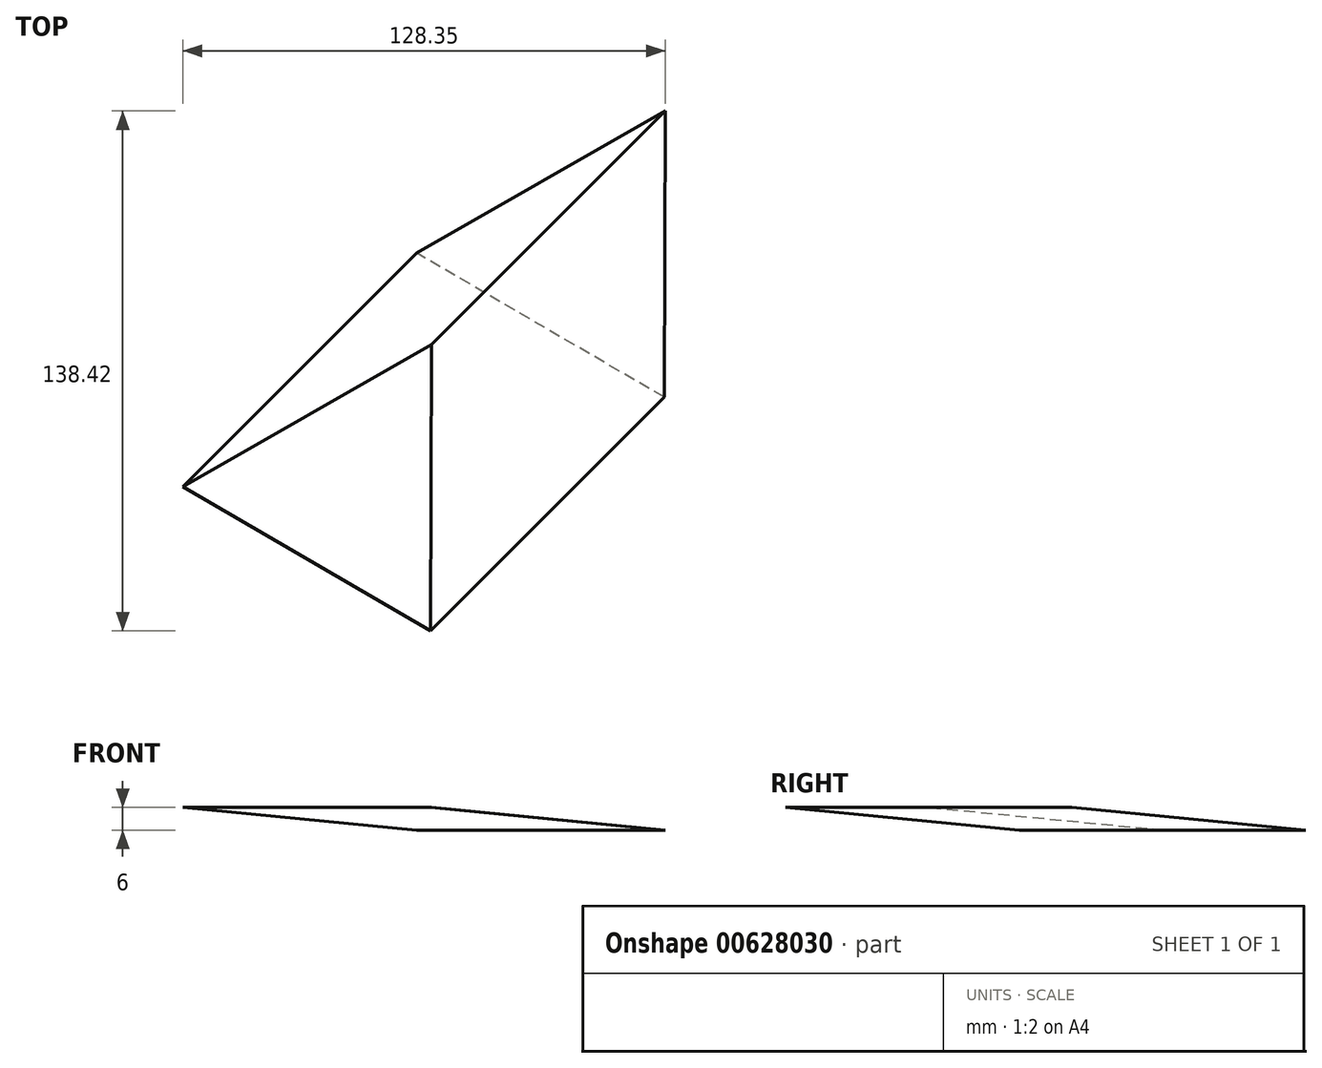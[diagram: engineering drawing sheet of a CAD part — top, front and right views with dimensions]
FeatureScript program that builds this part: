
annotation { "Feature Type Name" : "Feature", "Feature Type Description" : "" }
export const myFeature = defineFeature(function(context is Context, id is Id, definition is map)
    precondition{}
    {
        {
            assignVariable(context, id + "F0", {"name" : "l", "anyValue" : 6});
        }
        {
            var Q0;
            Q0=qCreatedBy(makeId("Top.planeOp"),FACE);
            var sketch = newSketch(context, id + "F1", { "sketchPlane" : qUnion([Q0])});
            skCircle(sketch, "E0.cCircle", {"center": v(0, 0) * mm, "radius": 22 * mm, "construction": true});
            skLineSegment(sketch, "E0.0", {"start": v(22.14, 38.02) * mm, "end": v(21.86, -38.18) * mm});
            skLineSegment(sketch, "E0.1", {"start": v(21.86, -38.18) * mm, "end": v(-44, 0.16) * mm});
            skLineSegment(sketch, "E0.2", {"start": v(-44, 0.16) * mm, "end": v(22.14, 38.02) * mm});
            skPoint(sketch, "E0.0.midPoint", {"position": v(22, -0.08) * mm});
            skSolve(sketch);
        }
        {
            var Q0;
            Q0=qCreatedBy(makeId("Right.planeOp"),FACE);
            var Q1;
            Q1=qCreatedBy(makeId("Front.planeOp"),FACE);
            cPlane(context, id + "F2", {"entities" : qUnion([Q0, Q1]), "cplaneType" : CPlaneType.MID_PLANE, "offset" : 25.4 * mm, "flipAlignment" : true, "width" : 152.4 * mm, "height" : 152.4 * mm});
        }
        {
            var Q0;
            Q0=qCreatedBy(makeId("Top.planeOp"),FACE);
            cPlane(context, id + "F3", {"entities" : qUnion([Q0]), "cplaneType" : CPlaneType.OFFSET, "offset" : (getVariable(context, 'l')) * mm, "width" : 152.4 * mm, "height" : 152.4 * mm});
        }
        {
            var Q0;
            Q0=qCreatedBy(id+"F2.planeOp",FACE);
            var sketch = newSketch(context, id + "F4", { "sketchPlane" : qUnion([Q0])});
            skLineSegment(sketch, "E1", {"start": v(0, 0) * mm, "end": v(-88.31, 152.96) * mm});
            skSolve(sketch);
        }
        {
            var Q0;
            Q0=qCreatedBy(id+"F3.planeOp",FACE);
            var sketch = newSketch(context, id + "F5", { "sketchPlane" : qUnion([Q0])});
            skLineSegment(sketch, "E2.0", {"start": v(-40.08, -24.2) * mm, "end": v(-40.36, -100.4) * mm});
            skLineSegment(sketch, "E3.0", {"start": v(-106.21, -62.05) * mm, "end": v(-40.08, -24.2) * mm});
            skLineSegment(sketch, "E4.0", {"start": v(-40.36, -100.4) * mm, "end": v(-106.21, -62.05) * mm});
            skCircle(sketch, "E5.0", {"center": v(-62.22, -62.22) * mm, "radius": 22 * mm, "construction": true});
            skSolve(sketch);
        }
        {
            var Q0;
            Q0=makeQuery(id+"F5.imprint","IMPRINT",FACE,{"disambiguationData":[TD([[makeQuery(id+"F5.imprint","IMPRINT",EDGE,{"derivedFrom":sQuery(id+"F5.wireOp",EDGE,"E2.0")}),-1.0]])]});
            var Q1;
            Q1=makeQuery(id+"F1.imprint","IMPRINT",FACE,{"disambiguationData":[TD([[makeQuery(id+"F1.imprint","IMPRINT",EDGE,{"derivedFrom":sQuery(id+"F1.wireOp",EDGE,"E0.0")}),-1.0]])]});
            var Q2;
            Q2=makeQuery(id+"F5.imprint","IMPRINT",FACE,{"disambiguationData":[TD([[makeQuery(id+"F5.imprint","IMPRINT",EDGE,{"derivedFrom":sQuery(id+"F5.wireOp",EDGE,"E2.0")}),-1.0]])]});
            var Q3;
            Q3=makeQuery(id+"F1.imprint","IMPRINT",FACE,{"disambiguationData":[TD([[makeQuery(id+"F1.imprint","IMPRINT",EDGE,{"derivedFrom":sQuery(id+"F1.wireOp",EDGE,"E0.0")}),-1.0]])]});
            var Q4;
            Q4=sQuery(id+"F1.wireOp",VERTEX,"E0.0.start");
            var Q5;
            Q5=sQuery(id+"F5.wireOp",VERTEX,"E3.0.end");
            var Q6;
            Q6=sQuery(id+"F1.wireOp",VERTEX,"E0.2.start");
            var Q7;
            Q7=sQuery(id+"F5.wireOp",VERTEX,"E4.0.end");
            var Q8;
            Q8=sQuery(id+"F1.wireOp",VERTEX,"E0.1.start");
            var Q9;
            Q9=sQuery(id+"F5.wireOp",VERTEX,"E4.0.start");
            loft(context, id + "F6", {"sheetProfilesArray" : [{ "sheetProfileEntities" : qUnion([Q0]) }, { "sheetProfileEntities" : qUnion([Q1]) }], "wireProfilesArray" : [{ "wireProfileEntities" : qUnion([Q2]) }, { "wireProfileEntities" : qUnion([Q3]) }], "connections" : [{ "connectionEntities" : qUnion([Q4, Q5, Q6, Q7, Q8, Q9]), "connectionEdgeQueries" : qUnion([]), "connectionEdgeParameters" : [] }]});
        }
        {
            var Q0;
            Q0=qCreatedBy(id+"F3.planeOp",FACE);
            var Q1;
            Q1=qCreatedBy(makeId("Top.planeOp"),FACE);
            cPlane(context, id + "F7", {"entities" : qUnion([Q0, Q1]), "cplaneType" : CPlaneType.MID_PLANE, "offset" : 25.4 * mm, "width" : 152.4 * mm, "height" : 152.4 * mm});
        }
        {
            var Q0;
            Q0=qCreatedBy(id+"F7.planeOp",FACE);
            var sketch = newSketch(context, id + "F8", { "sketchPlane" : qUnion([Q0])});
            skCircle(sketch, "E6", {"center": v(-31.1, -31.1) * mm, "radius": 12.7 * mm});
            skSolve(sketch);
        }
        {
            var Q0;
            Q0=sQuery(id+"F1.wireOp",EDGE,"E0.0");
            cPoint(context, id + "F9", {"entities" : qUnion([Q0]), "parameter" : 0.5});
        }
        {
            var Q0;
            Q0=sQuery(id+"F1.wireOp",EDGE,"E0.cCircle");
            var Q1;
            Q1 = qCreatedBy(id + "F9" ,VERTEX);
            cPlane(context, id + "F10", {"entities" : qUnion([Q0, Q1]), "cplaneType" : CPlaneType.CURVE_POINT, "offset" : 25.4 * mm, "width" : 152.4 * mm, "height" : 152.4 * mm});
        }
        {
            var Q0;
            Q0=qCreatedBy(id+"F10.planeOp",FACE);
            var sketch = newSketch(context, id + "F11", { "sketchPlane" : qUnion([Q0])});
            skPoint(sketch, "E7.0", {"position": v(39.99, 152.4) * mm});
            skPoint(sketch, "E8.0", {"position": v(-22, 0) * mm});
            skLineSegment(sketch, "E9", {"start": v(39.99, 152.4) * mm, "end": v(-22, 0) * mm, "construction": true});
            skLineSegment(sketch, "E10", {"start": v(39.99, 152.4) * mm, "end": v(-139.3, 152.4) * mm});
            skLineSegment(sketch, "E11", {"start": v(-139.3, 152.4) * mm, "end": v(-139.3, 0) * mm});
            skLineSegment(sketch, "E12", {"start": v(-139.3, 0) * mm, "end": v(-22, 0) * mm});
            skArc(sketch, "E13", {"start": v(-22, 0) * mm, "mid": v(16.99, 72.95) * mm, "end": v(39.99, 152.4) * mm});
            skPoint(sketch, "E14.0.start.orphan", {"position": v(18.3, 76.2) * mm});
            skSolve(sketch);
        }
        {
            var Q0;
            Q0=makeQuery(id+"F11.imprint","IMPRINT",FACE,{"disambiguationData":[TD([[makeQuery(id+"F11.imprint","IMPRINT",EDGE,{"derivedFrom":sQuery(id+"F11.wireOp",EDGE,"E10")}),1.0]])]});
            extrude(context, id + "F12", {"entities" : qUnion([Q0]), "operationType" : NewBodyOperationType.REMOVE, "endBound" : BoundingType.SYMMETRIC, "oppositeDirection" : true, "depth" : 227.08 * mm, "offsetDistance" : 25.4 * mm});
        }
    });
